# Revit family: TEMID_Турникет_трипод_TS2200
name_source: partatom
category: Электрооборудование
units: mm (PartAtom-declared; Revit-internal decimal feet)

## family parameters
Всегда вертикально = Нет
На основе рабочей плоскости = Нет
Общий = Да
При загрузке вырезать с полостями = Нет
Размер круглого соединителя = Использовать диаметр
Тип детали = Другая панель
Точка расчета площади = Нет

## types (1)
- TS2200 Pro
    ADSK_Группирование = 3. Периферийное оборудование
    ADSK_Единица измерения = шт.
    ADSK_Завод-изготовитель = TEMID
    ADSK_Количество = 1
    ADSK_Количество фаз = 1
    ADSK_Коэффициент мощности = 0.95
    ADSK_Марка = TS2200 Pro
    ADSK_Наименование = Турникет-трипод тумбовый, двухсторонний, нержавеющая сталь, идикатор направления прохода. Планки «антипаника», вход для кнопки аварийной разблокировки. Рабочая температура -28°C - +60°C. Вес — 65 кг.
    ADSK_Напряжение = 220 В
    ADSK_Номинальная мощность = 60 Вт
    ADSK_Полная мощность = 57 В·А
    ADSK_Размер_Высота = 980 мм
    ADSK_Размер_Глубина = 1110 мм
    ADSK_Размер_Ширина = 320 мм
    ADSK_Тип = TS2200 Pro
    ADSK_Ток = 0 А
    URL = https://temid-global.ru
    Высота основания = 50 мм
    Высота поручня = 300 мм
    Материал = Серый
    Отметка по умолчанию = 0 мм
    Тип трипода = TEMID_ВЛ_НО_Трипод : Трипод
    Трипод правый_Видимость = Да
